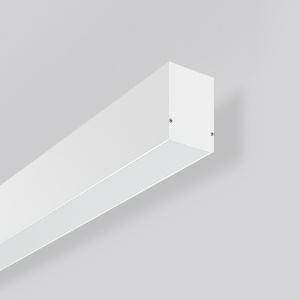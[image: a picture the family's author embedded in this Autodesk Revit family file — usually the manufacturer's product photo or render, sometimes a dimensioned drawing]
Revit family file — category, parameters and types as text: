
# Revit family: less_is_more_50_312612_002_76_307f
name_source: partatom
category: Lighting Fixtures
units: mm (PartAtom-declared; Revit-internal decimal feet)

## family parameters
Cut with Voids When Loaded = No
Host = Face
Light Source = No
Part Type = Normal
Room Calculation Point = No
Round Connector Dimension = Use Diameter
Shared = No

## types (1)
- LESS IS MORE 50 (1 x LED Modul 830, 3900 lm, 3000)
    Apparent Load = 30 VA
    CIE Flux Codes = 48 80 96 50 100
    Color Rendering = 80
    Color Temperature = 3000
    Default Elevation = 1800 mm
    Description = Series: LESS IS MORE 50
Linear wall luminaires. Housing: extruded aluminium profile, powder-coated. End cap aluminium powder-coated. Diffuser made of non-yellowing plastic (PMMA), opal. Direct 50%, indirect 50% light emission. Suitable for Wall (surface). LED unit with integrated converter interchangeable and removable. Suitable for through-wiring. With sensors or as a safety luminaire on request. 
Colour: traffic white, matt (RAL 9016)
Length: 1687 mm
Width: 67 mm
Height: 75 mm
Lamp: LED
Socket: without socket
Colour temperature: 3000K
Colour rendering index (CRI): 80
Light source: LED
Socket lamp2: Without base
Colour temperature: 3000K
Colour rendering index (CRI) 2: 80
System power: 30 W
Rated luminous flux: 3900 lm
Luminous efficiency: 130 lm/W
Control gear: Converter, dimmable, DALI
Control gear: Converter, dimmable, DALI
Protection class: I
Type of protection: IP 20
    Height = 75 mm
    Lamp = 1 x LED Modul 830
    Lamp Light Flux = 3900 lm
    Lamp count = 1
    Length = 1687 mm
    Lifetime = 50000 h
    Luminous efficacy = 130 lm/W
    Manufacturer = RZB
    ModVariant = No
    Model = 312612.002.76
    Mounting Place = Wall
    Mounting Type = Surface mounted
    Number of Poles = 1
    OnlyDefault = Yes
    Power Factor = 1
    Product Name = LESS IS MORE 50
    Product group = Surface mounted LED linear luminaires
    ProductGroupID = 2007
    Protection Class = Protection class I
    Protection Degree = IP 20
    RLX_Detail_Level = 1
    RLX_Emergency_Light_Flux = 0 lm
    RLX_Emergency_Type = 0
    RLX_Emergency_Type_DB = No
    RlxData = <blob elided: 39597 chars, md5=37b08e30>
    Socket = socket
    Standby Power = 0 W
    System Light Flux = 3900 lm
    System Power = 30 W
    Type Comments = Product without accessories
    Type Image = 312606.002.jpg
    URL = http://relux.com
    VarID = ---
    Voltage = 0 V
    Weight = 0.00 kg
    Width = 67 mm

## geometry (parser evidence)
native form markers: Blend x4, Sweep x13
no freeform markers — native parametric forms only
